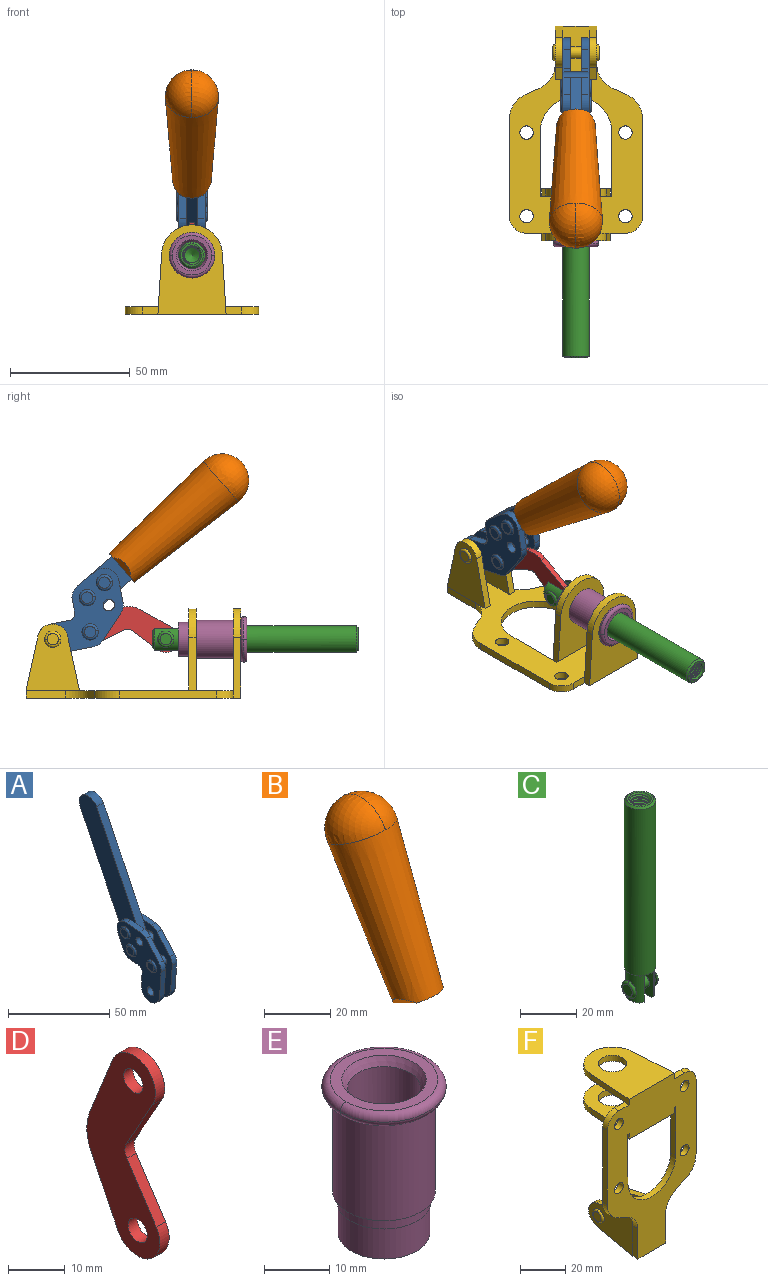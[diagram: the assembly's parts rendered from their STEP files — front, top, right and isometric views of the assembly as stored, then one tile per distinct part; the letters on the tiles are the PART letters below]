
ASSEMBLY  parts=6 mates=6
PART A: 59 faces, bbox 12.9x60.2x99.6 mm
  f0: torus R=2.39mm, axis (-1,0,0), area 14.9mm2, adj f20,f43,f51
  f1: torus R=2.39mm, axis (-1,0,0), area 14.9mm2, adj f19,f42,f51
  f2: torus R=2.39mm, axis (-1,0,0), area 14.9mm2, adj f18,f35,f51
  f3: torus R=2.39mm, axis (-1,0,0), area 14.9mm2, adj f14,f17,f23
  f4: torus R=2.39mm, axis (-1,0,0), area 14.9mm2, adj f13,f16,f23
  f5: torus R=2.39mm, axis (-1,0,0), area 14.9mm2, adj f12,f15,f23
  f6: cylinder r=2.39mm len=4.78mm, axis (1,0,0), area 46.5mm2, adj f48,f50,f51
  f7: cylinder r=2.39mm len=4.78mm, axis (1,0,0), area 46.5mm2, adj f50,f51
  f8: cylinder r=6.35mm len=12.68mm, axis (1,0,0), area 61.8mm2, adj f38,f39,f50,f51
  f9: cylinder r=2.39mm len=4.78mm, axis (-1,0,0), area 70.5mm2, adj f46,f50
  f10: cylinder r=2.39mm len=4.78mm, axis (-1,0,0), area 46.5mm2, adj f23,f45,f46
  f11: cylinder r=2.39mm len=4.78mm, axis (-1,0,0), area 46.5mm2, adj f23,f46
  f12: plane 4.78x4.78mm, normal (1,0,0), area 17.9mm2, adj f5,f15
  f13: plane 4.78x4.78mm, normal (1,0,0), area 17.9mm2, adj f4,f16
  f14: plane 4.78x4.78mm, normal (1,0,0), area 17.9mm2, adj f3,f17
  f15: torus R=2.39mm, axis (-1,0,0), area 14.9mm2, adj f5,f12,f23
  f16: torus R=2.39mm, axis (-1,0,0), area 14.9mm2, adj f4,f13,f23
  f17: torus R=2.39mm, axis (-1,0,0), area 14.9mm2, adj f3,f14,f23
  f18: plane 4.78x4.78mm, normal (-1,0,0), area 17.9mm2, adj f2,f35
  f19: plane 4.78x4.78mm, normal (-1,0,0), area 17.9mm2, adj f1,f42
  f20: plane 4.78x4.78mm, normal (-1,0,0), area 17.9mm2, adj f0,f43
  f21: plane 2.26x0.2mm, normal (1,0,0), area 0.2mm2, adj f31,f44
  f22: plane 2.26x0.2mm, normal (-1,0,0), area 0.2mm2, adj f41,f44
  f23: plane 39.37x30.77mm, normal (1,0,0), area 565.5mm2, adj f3,f4,f5,f10,f11,f15,f16,f17
  f24: cylinder r=6.1mm len=4.15mm, axis (-1,0,0), area 14.7mm2, adj f23,f25,f32,f46
  f25: plane 10.25x9.01mm, normal (0,-0.75,0.66), area 42.3mm2, adj f23,f24,f26,f46
  f26: cylinder r=6.35mm len=4.64mm, axis (-1,0,0), area 15.6mm2, adj f23,f25,f27,f46
  f27: plane 15.84x3.1mm, normal (0,-1,-0.07), area 49.2mm2, adj f23,f26,f28,f46
  f28: cylinder r=6.35mm len=12.68mm, axis (-1,0,0), area 61.8mm2, adj f23,f27,f29,f46
  f29: plane 8.11x3.1mm, normal (0,1,0.07), area 25.2mm2, adj f23,f28,f30,f46
  f30: cylinder r=3.05mm len=3.25mm, axis (-1,0,0), area 14.8mm2, adj f23,f29,f31,f46
  f31: plane 5.99x3.1mm, normal (0,0.07,-1), area 18.6mm2, adj f21,f23,f30,f44,f46
  f32: plane 9.5x3.1mm, normal (0,-0.07,1), area 29.5mm2, adj f23,f24,f33,f46,f47
  f33: cylinder r=6.1mm len=8.63mm, axis (-1,0,0), area 39.1mm2, adj f23,f32,f34,f47
  f34: plane 8.65x3.96mm, normal (0,0.91,-0.42), area 29.5mm2, adj f23,f33,f44,f47
  f35: torus R=2.39mm, axis (-1,0,0), area 14.9mm2, adj f2,f18,f51
  f36: plane 10.25x9.01mm, normal (0,-0.75,0.66), area 42.3mm2, adj f37,f49,f50,f51
  f37: cylinder r=6.35mm len=4.64mm, axis (1,0,0), area 15.6mm2, adj f36,f38,f50,f51
  f38: plane 15.84x3.1mm, normal (0,-1,-0.07), area 49.2mm2, adj f8,f37,f50,f51
  f39: plane 8.11x3.1mm, normal (0,1,0.07), area 25.2mm2, adj f8,f40,f50,f51
  f40: cylinder r=3.05mm len=3.25mm, axis (1,0,0), area 14.8mm2, adj f39,f41,f50,f51
  f41: plane 5.99x3.1mm, normal (0,0.07,-1), area 18.6mm2, adj f22,f40,f44,f50,f51
  f42: torus R=2.39mm, axis (-1,0,0), area 14.9mm2, adj f1,f19,f51
  f43: torus R=2.39mm, axis (-1,0,0), area 14.9mm2, adj f0,f20,f51
  f44: cylinder r=6.35mm len=12.12mm, axis (-1,0,0), area 128.9mm2, adj f21,f22,f23,f31,f34,f41,f46,f47
  f45: plane 2.65x1.35mm, normal (1,0,0), area 1mm2, adj f10,f55
  f46: plane 39.08x20.42mm, normal (-1,0,0), area 412.5mm2, adj f9,f10,f11,f24,f25,f26,f27,f28
  f47: plane 77.62x39.82mm, normal (1,0,0), area 850mm2, adj f32,f33,f34,f44,f53,f54,f55
  f48: plane 2.65x1.35mm, normal (-1,0,0), area 1mm2, adj f6,f55
  f49: cylinder r=6.1mm len=4.15mm, axis (1,0,0), area 14.7mm2, adj f36,f50,f51,f56
  f50: plane 39.08x20.42mm, normal (1,0,0), area 412.5mm2, adj f6,f7,f8,f9,f36,f37,f38,f39
  f51: plane 39.37x30.77mm, normal (-1,0,0), area 565.5mm2, adj f0,f1,f2,f6,f7,f8,f35,f36
  f52: plane 8.65x3.96mm, normal (0,0.91,-0.42), area 29.5mm2, adj f44,f51,f57,f58
  f53: plane 68.49x33.4mm, normal (0,0.9,-0.44), area 358.1mm2, adj f44,f47,f54,f58
  f54: cylinder r=6.35mm len=12.06mm, axis (1,0,0), area 93.7mm2, adj f47,f53,f55,f58
  f55: plane 68.49x33.4mm, normal (0,-0.9,0.44), area 358.1mm2, adj f44,f45,f46,f47,f48,f50,f54,f58
  f56: plane 9.5x3.1mm, normal (0,-0.07,1), area 29.5mm2, adj f49,f50,f51,f57,f58
  f57: cylinder r=6.1mm len=8.63mm, axis (1,0,0), area 39.1mm2, adj f51,f52,f56,f58
  f58: plane 77.62x39.82mm, normal (-1,0,0), area 850mm2, adj f44,f52,f53,f54,f55,f56,f57
PART B: 11 faces, bbox 22.3x42.6x64.5 mm
  f0: sphere r=11.13mm, area 411.4mm2, adj f1,f8
  f1: cone r=11.11mm half-angle=3.3deg, axis (0,0.44,0.9), area 3251.8mm2, adj f0,f7,f8,f9,f10
  f2: cylinder r=6.16mm len=11.7mm, axis (1,0,0), area 89.5mm2, adj f3,f4,f5,f6
  f3: plane 60.23x36.75mm, normal (-1,0,0), area 763.6mm2, adj f2,f4,f6,f10
  f4: plane 51.37x25.05mm, normal (0,0.9,-0.44), area 264.2mm2, adj f2,f3,f5,f10
  f5: plane 60.23x36.75mm, normal (1,0,0), area 763.6mm2, adj f2,f4,f6,f10
  f6: plane 51.37x25.05mm, normal (0,-0.9,0.44), area 264.2mm2, adj f2,f3,f5,f10
  f7: plane 9.95x5.95mm, normal (0.71,-0.31,-0.64), area 25.8mm2, adj f1,f10
  f8: sphere r=11.13mm, area 411.4mm2, adj f0,f1
  f9: plane 9.95x5.95mm, normal (-0.71,-0.31,-0.64), area 25.8mm2, adj f1,f10
  f10: plane 14.27x11.38mm, normal (0,-0.44,-0.9), area 106.7mm2, adj f1,f3,f4,f5,f6,f7,f9
PART C: 48 faces, bbox 12.6x11.1x86.1 mm
  f0: torus R=2.41mm, axis (-1,0,0), area 15mm2, adj f30,f32,f34
  f1: torus R=2.41mm, axis (-1,0,0), area 15mm2, adj f29,f31,f33
  f2: cylinder r=5.54mm len=72.39mm, axis (0,0,1), area 2518.5mm2, adj f3,f4,f42,f43
  f3: cone r=5.54mm half-angle=45deg, axis (0,0,1), area 7.6mm2, adj f2,f5,f41
  f4: cone r=5.54mm half-angle=45deg, axis (0,0,-1), area 34.9mm2, adj f2,f39
  f5: cylinder r=5.08mm len=11.48mm, axis (0,0,1), area 108.3mm2, adj f3,f7,f8,f41
  f6: cylinder r=2.41mm len=4.83mm, axis (-1,0,0), area 71.2mm2, adj f40,f41
  f7: cylinder r=2.41mm len=4.83mm, axis (-1,0,0), area 7.6mm2, adj f5,f34
  f8: cone r=5.08mm half-angle=45deg, axis (0,0,1), area 10.6mm2, adj f5,f37,f41
  f9: cone r=3.98mm half-angle=45deg, axis (0,0,1), area 17.6mm2, adj f27,f39,f45,f46,f47
  f10: cylinder r=2.41mm len=4.83mm, axis (-1,0,0), area 7.6mm2, adj f33,f38
  f11: cylinder r=3.2mm len=6.4mm, axis (0,0,1), area 78.4mm2, adj f12,f28,f44,f45,f47
  f12: cylinder r=3.2mm len=6.4mm, axis (0,0,1), area 10.5mm2, adj f11,f13,f45,f47
  f13: cylinder r=3.2mm len=6.4mm, axis (0,0,1), area 10.5mm2, adj f12,f14,f45,f47
  f14: cylinder r=3.2mm len=6.4mm, axis (0,0,1), area 10.5mm2, adj f13,f15,f45,f47
  f15: cylinder r=3.2mm len=6.4mm, axis (0,0,1), area 10.5mm2, adj f14,f16,f45,f47
  f16: cylinder r=3.2mm len=6.4mm, axis (0,0,1), area 10.5mm2, adj f15,f17,f45,f47
  f17: cylinder r=3.2mm len=6.4mm, axis (0,0,1), area 10.5mm2, adj f16,f18,f45,f47
  f18: cylinder r=3.2mm len=6.4mm, axis (0,0,1), area 10.5mm2, adj f17,f19,f45,f47
  f19: cylinder r=3.2mm len=6.4mm, axis (0,0,1), area 10.5mm2, adj f18,f20,f45,f47
  f20: cylinder r=3.2mm len=6.4mm, axis (0,0,1), area 10.5mm2, adj f19,f21,f45,f47
  f21: cylinder r=3.2mm len=6.4mm, axis (0,0,1), area 10.5mm2, adj f20,f22,f45,f47
  f22: cylinder r=3.2mm len=6.4mm, axis (0,0,1), area 10.5mm2, adj f21,f23,f45,f47
  f23: cylinder r=3.2mm len=6.4mm, axis (0,0,1), area 10.5mm2, adj f22,f24,f45,f47
  f24: cylinder r=3.2mm len=6.4mm, axis (0,0,1), area 10.5mm2, adj f23,f25,f45,f47
  f25: cylinder r=3.2mm len=6.4mm, axis (0,0,1), area 10.5mm2, adj f24,f26,f45,f47
  f26: cylinder r=3.2mm len=6.4mm, axis (0,0,1), area 10.5mm2, adj f25,f27,f45,f47
  f27: cylinder r=3.2mm len=6.4mm, axis (0,0,1), area 7.4mm2, adj f9,f26,f45,f47
  f28: cone r=3.2mm half-angle=60deg, axis (0,0,1), area 37.2mm2, adj f11
  f29: plane 4.83x4.83mm, normal (-1,0,0), area 18.3mm2, adj f1,f31
  f30: plane 4.83x4.83mm, normal (1,0,0), area 18.3mm2, adj f0,f32
  f31: torus R=2.41mm, axis (-1,0,0), area 15mm2, adj f1,f29,f33
  f32: torus R=2.41mm, axis (-1,0,0), area 15mm2, adj f0,f30,f34
  f33: plane 6.83x6.83mm, normal (1,0,0), area 18.3mm2, adj f1,f10,f31
  f34: plane 6.83x6.83mm, normal (-1,0,0), area 18.3mm2, adj f0,f7,f32
  f35: cone r=5.08mm half-angle=45deg, axis (0,0,1), area 10.6mm2, adj f36,f38,f40
  f36: plane 7.25x1.97mm, normal (0,0,-1), area 10mm2, adj f35,f40
  f37: plane 7.25x1.97mm, normal (0,0,-1), area 10mm2, adj f8,f41
  f38: cylinder r=5.08mm len=11.48mm, axis (0,0,1), area 108.3mm2, adj f10,f35,f40,f42
  f39: plane 9.55x9.55mm, normal (0,0,1), area 22mm2, adj f4,f9
  f40: plane 12.76x10.09mm, normal (1,0,0), area 95.7mm2, adj f6,f35,f36,f38,f42,f43
  f41: plane 12.76x10.09mm, normal (-1,0,0), area 95.7mm2, adj f3,f5,f6,f8,f37,f43
  f42: cone r=5.54mm half-angle=45deg, axis (0,0,1), area 7.6mm2, adj f2,f38,f40
  f43: plane 11.07x4.7mm, normal (0,0,-1), area 50.4mm2, adj f2,f40,f41
  f44: plane 0.89x0.62mm, normal (-1,0,0), area 0.3mm2, adj f11,f45,f46,f47
  f45: bspline ~24.8x7.63mm, area 266.6mm2, adj f9,f11,f12,f13,f14,f15,f16,f17
  f46: bspline ~24.87x7.63mm, area 73.6mm2, adj f9,f44,f45,f47
  f47: bspline ~24.98x7.63mm, area 272.5mm2, adj f9,f11,f12,f13,f14,f15,f16,f17
PART D: 12 faces, bbox 2.3x18.2x42.8 mm
  f0: cylinder r=2.4mm len=4.8mm, axis (1,0,0), area 34.9mm2, adj f4,f11
  f1: cylinder r=10.41mm len=8.47mm, axis (1,0,0), area 20.2mm2, adj f4,f9,f10,f11
  f2: cylinder r=3.05mm len=3.16mm, axis (1,0,0), area 7.7mm2, adj f4,f6,f7,f11
  f3: cylinder r=2.4mm len=4.8mm, axis (1,0,0), area 34.9mm2, adj f4,f11
  f4: plane 42.81x18.23mm, normal (-1,0,0), area 414.1mm2, adj f0,f1,f2,f3,f5,f6,f7,f8
  f5: cylinder r=5.54mm len=10.67mm, axis (1,0,0), area 41.8mm2, adj f4,f6,f10,f11
  f6: plane 11.66x6.53mm, normal (0,-0.87,-0.49), area 30.9mm2, adj f2,f4,f5,f11
  f7: plane 11.17x7.33mm, normal (0,-0.84,0.55), area 30.9mm2, adj f2,f4,f8,f11
  f8: cylinder r=5.54mm len=10.51mm, axis (1,0,0), area 41.8mm2, adj f4,f7,f9,f11
  f9: plane 13.67x6.67mm, normal (0,0.9,-0.44), area 35.1mm2, adj f1,f4,f8,f11
  f10: plane 14.1x5.7mm, normal (0,0.93,0.37), area 35.1mm2, adj f1,f4,f5,f11
  f11: plane 42.81x18.23mm, normal (1,0,0), area 414.1mm2, adj f0,f1,f2,f3,f5,f6,f7,f8
PART E: 15 faces, bbox 20.6x20.6x28.7 mm
  f0: torus R=8.26mm, axis (0,0,1), area 56.8mm2, adj f1,f10,f12
  f1: torus R=8.26mm, axis (0,0,1), area 56.8mm2, adj f0,f6,f13
  f2: cylinder r=5.59mm len=25.91mm, axis (0,0,1), area 909.6mm2, adj f3,f4
  f3: cone r=6.86mm half-angle=45deg, axis (0,0,-1), area 70.2mm2, adj f2,f14
  f4: cone r=6.47mm half-angle=30deg, axis (0,0,1), area 66.7mm2, adj f2,f13
  f5: cylinder r=7.04mm len=14.07mm, axis (0,0,1), area 252.6mm2, adj f11,f14
  f6: torus R=8.26mm, axis (0,0,1), area 56.8mm2, adj f1,f12,f13
  f7: cylinder r=7.16mm len=14.33mm, axis (0,0,1), area 91.5mm2, adj f9,f11
  f8: cylinder r=7.86mm len=18.42mm, axis (0,0,1), area 909.6mm2, adj f9,f10
  f9: plane 15.72x15.72mm, normal (0,0,-1), area 33mm2, adj f7,f8
  f10: plane 16.51x16.51mm, normal (0,0,-1), area 19.9mm2, adj f0,f8,f12
  f11: plane 14.33x14.33mm, normal (0,0,-1), area 5.7mm2, adj f5,f7
  f12: torus R=8.26mm, axis (0,0,1), area 56.8mm2, adj f0,f6,f10
  f13: plane 16.51x16.51mm, normal (0,0,1), area 82.7mm2, adj f1,f4,f6
  f14: plane 14.07x14.07mm, normal (0,0,-1), area 7.8mm2, adj f3,f5
PART F: 55 faces, bbox 55.7x37.4x89.8 mm
  f0: torus R=2.41mm, axis (-1,0,0), area 15mm2, adj f11,f15,f25
  f1: torus R=2.41mm, axis (-1,0,0), area 15mm2, adj f10,f12,f22
  f2: cylinder r=2.78mm len=5.56mm, axis (0,-1,0), area 54.2mm2, adj f30,f54
  f3: cylinder r=14.99mm len=29.97mm, axis (0,-1,0), area 145.9mm2, adj f30,f49,f53,f54
  f4: cylinder r=2.78mm len=5.56mm, axis (0,-1,0), area 54.2mm2, adj f30,f54
  f5: cylinder r=2.78mm len=5.56mm, axis (0,-1,0), area 54.2mm2, adj f30,f54
  f6: cylinder r=2.78mm len=5.56mm, axis (0,-1,0), area 54.2mm2, adj f30,f54
  f7: cylinder r=6.35mm len=12.7mm, axis (0,0,1), area 123.6mm2, adj f27,f51
  f8: cylinder r=6.35mm len=12.7mm, axis (0,0,-1), area 124.7mm2, adj f21,f35
  f9: cylinder r=2.41mm len=11.18mm, axis (-1,0,0), area 169.4mm2, adj f16,f19
  f10: plane 4.83x4.83mm, normal (1,0,0), area 18.3mm2, adj f1,f12
  f11: plane 4.83x4.83mm, normal (-1,0,0), area 18.3mm2, adj f0,f15
  f12: torus R=2.41mm, axis (-1,0,0), area 15mm2, adj f1,f10,f22
  f13: cylinder r=6.35mm len=12.41mm, axis (1,0,0), area 53.4mm2, adj f18,f19,f22,f23
  f14: cylinder r=6.35mm len=12.41mm, axis (-1,0,0), area 53.4mm2, adj f16,f17,f24,f25
  f15: torus R=2.41mm, axis (-1,0,0), area 15mm2, adj f0,f11,f25
  f16: plane 27.86x22.35mm, normal (1,0,0), area 425.4mm2, adj f9,f14,f17,f24,f30
  f17: plane 22.86x4.97mm, normal (0,0.21,0.98), area 72.5mm2, adj f14,f16,f25,f30
  f18: plane 22.86x4.97mm, normal (0,0.21,0.98), area 72.5mm2, adj f13,f19,f22,f30
  f19: plane 27.86x22.35mm, normal (-1,0,0), area 425.4mm2, adj f9,f13,f18,f23,f30
  f20: cylinder r=12.7mm len=25.35mm, axis (0,0,-1), area 119.8mm2, adj f21,f34,f35,f36
  f21: plane 34.21x28.07mm, normal (0,0,-1), area 702.4mm2, adj f8,f20,f30,f34,f36
  f22: plane 27.96x22.45mm, normal (1,0,0), area 407.2mm2, adj f1,f12,f13,f18,f23,f30,f42,f43
  f23: plane 22.86x4.97mm, normal (0,0.21,-0.98), area 72.5mm2, adj f13,f19,f22,f44
  f24: plane 22.86x4.97mm, normal (0,0.21,-0.98), area 72.5mm2, adj f14,f16,f25,f44
  f25: plane 27.86x22.35mm, normal (-1,0,0), area 407.1mm2, adj f0,f14,f15,f17,f24,f30,f45,f46
  f26: plane 3.1x0.95mm, normal (0,0,-1), area 2.7mm2, adj f30,f49,f50,f54
  f27: plane 34.21x28.07mm, normal (0,0,1), area 702.4mm2, adj f7,f28,f30,f50,f52
  f28: cylinder r=12.7mm len=25.35mm, axis (0,0,1), area 118.8mm2, adj f27,f50,f51,f52
  f29: plane 3.1x0.95mm, normal (0,0,-1), area 2.7mm2, adj f30,f52,f53,f54
  f30: plane 86.54x55.63mm, normal (0,1,0), area 2362.9mm2, adj f2,f3,f4,f5,f6,f16,f17,f18
  f31: plane 40.56x3.1mm, normal (-1,0,0), area 125.7mm2, adj f30,f32,f48,f54
  f32: cylinder r=7.11mm len=7.11mm, axis (0,-1,0), area 34.6mm2, adj f30,f31,f33,f54
  f33: plane 6.67x3.1mm, normal (0,0,1), area 20.4mm2, adj f30,f32,f34,f54
  f34: plane 25.39x3.13mm, normal (-1,0.06,0), area 79.5mm2, adj f20,f21,f33,f35,f54
  f35: plane 37.31x28.45mm, normal (0,0,1), area 789.9mm2, adj f8,f20,f34,f36,f54
  f36: plane 25.39x3.13mm, normal (1,0.06,0), area 79.5mm2, adj f20,f21,f35,f37,f54
  f37: plane 6.67x3.1mm, normal (0,0,1), area 20.4mm2, adj f30,f36,f38,f54
  f38: cylinder r=7.11mm len=7.11mm, axis (0,-1,0), area 34.6mm2, adj f30,f37,f39,f54
  f39: plane 40.56x3.1mm, normal (1,0,0), area 125.7mm2, adj f30,f38,f40,f54
  f40: cylinder r=11.18mm len=10.16mm, axis (0,-1,0), area 39.5mm2, adj f30,f39,f41,f54
  f41: plane 6.09x3.1mm, normal (0.42,0,-0.91), area 20.8mm2, adj f30,f40,f42,f54
  f42: cylinder r=11.18mm len=9.41mm, axis (0,-1,0), area 37.2mm2, adj f22,f30,f41,f43,f54
  f43: plane 16.5x3.1mm, normal (1,0,0), area 51.1mm2, adj f22,f42,f44,f54
  f44: plane 17.37x3.1mm, normal (0,0,-1), area 53.8mm2, adj f23,f24,f30,f43,f45,f54
  f45: plane 16.5x3.1mm, normal (-1,0,0), area 51.1mm2, adj f25,f44,f46,f54
  f46: cylinder r=11.18mm len=9.41mm, axis (0,-1,0), area 37.2mm2, adj f25,f30,f45,f47,f54
  f47: plane 6.09x3.1mm, normal (-0.42,0,-0.91), area 20.8mm2, adj f30,f46,f48,f54
  f48: cylinder r=11.18mm len=10.16mm, axis (0,-1,0), area 39.5mm2, adj f30,f31,f47,f54
  f49: plane 26.54x3.1mm, normal (-1,0,0), area 82.3mm2, adj f3,f26,f30,f54
  f50: plane 25.39x3.1mm, normal (1,0.06,0), area 78.8mm2, adj f26,f27,f28,f51,f54
  f51: plane 37.31x28.45mm, normal (0,0,-1), area 789.9mm2, adj f7,f28,f50,f52,f54
  f52: plane 25.39x3.1mm, normal (-1,0.06,0), area 78.8mm2, adj f27,f28,f29,f51,f54
  f53: plane 26.54x3.1mm, normal (1,0,0), area 82.3mm2, adj f3,f29,f30,f54
  f54: plane 89.66x55.63mm, normal (0,-1,0), area 2678.5mm2, adj f2,f3,f4,f5,f6,f26,f29,f31
PLACE A rot(axis=(1,0,0),75deg) t=(0,3.86,9.14)mm
PLACE B rot(axis=(1,0,0),75deg) t=(-0.04,3.86,9.14)mm
PLACE C rot(axis=(1,0,0),90deg) t=(0,9.52,0)mm
PLACE D rot(axis=(0,-0.69,-0.73),180deg) t=(0,11.7,2.14)mm
PLACE E rot(axis=(1,0,0),90deg) t=(0,9.14,0)mm
PLACE F rot(axis=(1,0,0),90deg) t=(0,9.14,0)mm fixed
MATE slider C.f2 <-> E.f2  axis (0,-1,0) through (0,-49.26,24.61)mm
MATE fastened E.f0 <-> F.f7  axis (0,1,0) through (0,-37.25,24.61)mm
MATE revolute D.f3 <-> C.f6  axis (-1,0,0) through (0,-5.96,24.61)mm
MATE fastened B.f2 <-> A.f54  axis (1,0,0) through (-2.35,-30.66,91.94)mm
MATE revolute A.f7 <-> F.f0  axis (1,0,0) through (0,41.23,24.61)mm
MATE revolute D.f5 <-> A.f4  axis (-1,0,0) through (0,25.65,27.64)mm
